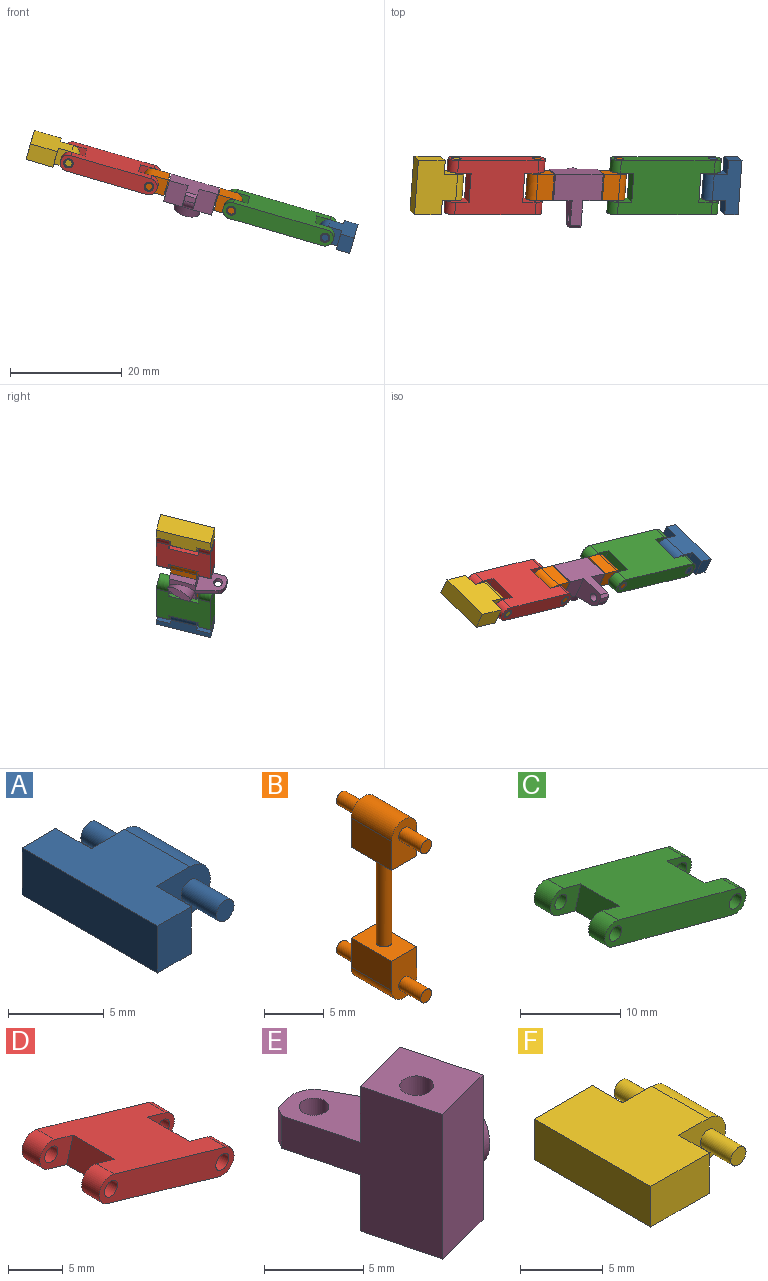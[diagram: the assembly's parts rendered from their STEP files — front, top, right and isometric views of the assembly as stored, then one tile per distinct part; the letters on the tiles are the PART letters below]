
ASSEMBLY  parts=6 mates=15
PART A: 14 faces, bbox 6.5x10x3 mm
  f0: plane 3x2.6mm, normal (1,0,0), area 7.8mm2, adj f2,f4,f6,f11
  f1: plane 3x2.6mm, normal (1,0,0), area 7.8mm2, adj f2,f4,f5,f10
  f2: plane 10x5mm, normal (0,0,1), area 37mm2, adj f0,f1,f3,f5,f6,f9,f10,f11
  f3: plane 10x3mm, normal (-1,0,0), area 30mm2, adj f2,f4,f5,f6
  f4: plane 10x5mm, normal (0,0,-1), area 37mm2, adj f0,f1,f3,f5,f6,f9,f10,f11
  f5: plane 3x2.5mm, normal (0,-1,0), area 7.5mm2, adj f1,f2,f3,f4
  f6: plane 3x2.5mm, normal (0,1,0), area 7.5mm2, adj f0,f2,f3,f4
  f7: cylinder r=0.65mm len=2.6mm, axis (0,1,0), area 10.6mm2, adj f8,f10
  f8: plane 1.3x1.3mm, normal (0,-1,0), area 1.3mm2, adj f7
  f9: cylinder r=1.5mm len=4.8mm, axis (0,1,0), area 22.6mm2, adj f2,f4,f10,f11
  f10: plane 4x3mm, normal (0,-1,0), area 9.7mm2, adj f1,f2,f4,f7,f9
  f11: plane 4x3mm, normal (0,1,0), area 9.7mm2, adj f0,f2,f4,f9,f13
  f12: plane 1.3x1.3mm, normal (0,1,0), area 1.3mm2, adj f13
  f13: cylinder r=0.65mm len=2.6mm, axis (0,1,0), area 10.6mm2, adj f11,f12
PART B: 21 faces, bbox 3x10x18.3 mm
  f0: cylinder r=0.65mm len=9.34mm, axis (0,0,-1), area 38.2mm2, adj f4,f14
  f1: plane 4.8x3mm, normal (1,0,0), area 14.4mm2, adj f2,f4,f5,f6
  f2: cylinder r=1.5mm len=4.8mm, axis (0,1,0), area 22.6mm2, adj f1,f3,f5,f6
  f3: plane 4.8x3mm, normal (-1,0,0), area 14.4mm2, adj f2,f4,f5,f6
  f4: plane 4.8x3mm, normal (0,0,-1), area 13.1mm2, adj f0,f1,f3,f5,f6
  f5: plane 4.5x3mm, normal (0,-1,0), area 11.2mm2, adj f1,f2,f3,f4,f10
  f6: plane 4.5x3mm, normal (0,1,0), area 11.2mm2, adj f1,f2,f3,f4,f8
  f7: plane 1.3x1.3mm, normal (0,1,0), area 1.3mm2, adj f8
  f8: cylinder r=0.65mm len=2.6mm, axis (0,1,0), area 10.6mm2, adj f6,f7
  f9: plane 1.3x1.3mm, normal (0,-1,0), area 1.3mm2, adj f10
  f10: cylinder r=0.65mm len=2.6mm, axis (0,1,0), area 10.6mm2, adj f5,f9
  f11: plane 4.8x3mm, normal (-1,0,0), area 14.4mm2, adj f12,f14,f15,f16
  f12: cylinder r=1.5mm len=4.8mm, axis (0,1,0), area 22.6mm2, adj f11,f13,f15,f16
  f13: plane 4.8x3mm, normal (1,0,0), area 14.4mm2, adj f12,f14,f15,f16
  f14: plane 4.8x3mm, normal (0,0,1), area 13.1mm2, adj f0,f11,f13,f15,f16
  f15: plane 4.5x3mm, normal (0,-1,0), area 11.2mm2, adj f11,f12,f13,f14,f20
  f16: plane 4.5x3mm, normal (0,1,0), area 11.2mm2, adj f11,f12,f13,f14,f18
  f17: plane 1.3x1.3mm, normal (0,1,0), area 1.3mm2, adj f18
  f18: cylinder r=0.65mm len=2.6mm, axis (0,1,0), area 10.6mm2, adj f16,f17
  f19: plane 1.3x1.3mm, normal (0,-1,0), area 1.3mm2, adj f20
  f20: cylinder r=0.65mm len=2.6mm, axis (0,1,0), area 10.6mm2, adj f15,f19
PART C: 18 faces, bbox 19.9x10x7.5 mm
  f0: plane 5.4x2.9mm, normal (-0.97,0,0.26), area 16.2mm2, adj f2,f3,f11,f17
  f1: plane 5.4x2.9mm, normal (0.97,0,-0.26), area 16.2mm2, adj f2,f3,f8,f14
  f2: plane 16.9x10mm, normal (0.26,0,0.97), area 148mm2, adj f0,f1,f4,f5,f6,f8,f9,f11
  f3: plane 16.9x10mm, normal (-0.26,0,-0.97), area 148mm2, adj f0,f1,f4,f5,f6,f8,f9,f11
  f4: plane 19.9x7.53mm, normal (0,-1,0), area 55mm2, adj f2,f3,f6,f7,f9,f10
  f5: plane 19.9x7.53mm, normal (0,1,0), area 55mm2, adj f2,f3,f12,f13,f15,f16
  f6: cylinder r=1.5mm len=2.95mm, axis (0,-1,0), area 10.8mm2, adj f2,f3,f4,f8
  f7: cylinder r=0.85mm len=2.3mm, axis (0,-1,0), area 12.3mm2, adj f4,f8
  f8: plane 4.3x3.6mm, normal (0,1,0), area 8.8mm2, adj f1,f2,f3,f6,f7
  f9: cylinder r=1.5mm len=2.95mm, axis (0,-1,0), area 10.8mm2, adj f2,f3,f4,f11
  f10: cylinder r=0.85mm len=2.3mm, axis (0,-1,0), area 12.3mm2, adj f4,f11
  f11: plane 4.3x3.6mm, normal (0,1,0), area 8.8mm2, adj f0,f2,f3,f9,f10
  f12: cylinder r=1.5mm len=2.95mm, axis (0,1,0), area 10.8mm2, adj f2,f3,f5,f14
  f13: cylinder r=0.85mm len=2.3mm, axis (0,1,0), area 12.3mm2, adj f5,f14
  f14: plane 4.3x3.6mm, normal (0,-1,0), area 8.8mm2, adj f1,f2,f3,f12,f13
  f15: cylinder r=1.5mm len=2.95mm, axis (0,1,0), area 10.8mm2, adj f2,f3,f5,f17
  f16: cylinder r=0.85mm len=2.3mm, axis (0,1,0), area 12.3mm2, adj f5,f17
  f17: plane 4.3x3.6mm, normal (0,-1,0), area 8.8mm2, adj f0,f2,f3,f15,f16
PART D: 18 faces, bbox 17.4x10x7.2 mm
  f0: plane 5.4x2.88mm, normal (-0.96,0,0.28), area 16.2mm2, adj f2,f3,f8,f14
  f1: plane 5.4x2.88mm, normal (0.96,0,-0.28), area 16.2mm2, adj f2,f3,f11,f17
  f2: plane 14.4x10mm, normal (0.28,0,0.96), area 123mm2, adj f0,f1,f4,f5,f6,f8,f9,f11
  f3: plane 14.4x10mm, normal (-0.28,0,-0.96), area 123mm2, adj f0,f1,f4,f5,f6,f8,f9,f11
  f4: plane 17.4x7.19mm, normal (0,-1,0), area 47.5mm2, adj f2,f3,f6,f7,f9,f10
  f5: plane 17.4x7.19mm, normal (0,1,0), area 47.5mm2, adj f2,f3,f12,f13,f15,f16
  f6: cylinder r=1.5mm len=2.94mm, axis (0,-1,0), area 10.8mm2, adj f2,f3,f4,f8
  f7: cylinder r=0.85mm len=2.3mm, axis (0,-1,0), area 12.3mm2, adj f4,f8
  f8: plane 4.32x3.64mm, normal (0,1,0), area 8.8mm2, adj f0,f2,f3,f6,f7
  f9: cylinder r=1.5mm len=2.94mm, axis (0,-1,0), area 10.8mm2, adj f2,f3,f4,f11
  f10: cylinder r=0.85mm len=2.3mm, axis (0,-1,0), area 12.3mm2, adj f4,f11
  f11: plane 4.32x3.64mm, normal (0,1,0), area 8.8mm2, adj f1,f2,f3,f9,f10
  f12: cylinder r=1.5mm len=2.94mm, axis (0,1,0), area 10.8mm2, adj f2,f3,f5,f14
  f13: cylinder r=0.85mm len=2.3mm, axis (0,1,0), area 12.3mm2, adj f5,f14
  f14: plane 4.32x3.64mm, normal (0,-1,0), area 8.8mm2, adj f0,f2,f3,f12,f13
  f15: cylinder r=1.5mm len=2.94mm, axis (0,1,0), area 10.8mm2, adj f2,f3,f5,f17
  f16: cylinder r=0.85mm len=2.3mm, axis (0,1,0), area 12.3mm2, adj f5,f17
  f17: plane 4.32x3.64mm, normal (0,-1,0), area 8.8mm2, adj f1,f2,f3,f15,f16
PART E: 18 faces, bbox 6.7x10x8.9 mm
  f0: plane 4.65x4.45mm, normal (0.97,0.25,0), area 12.6mm2, adj f2,f4,f7,f9,f15
  f1: plane 3.87x3.45mm, normal (-0.25,0.97,0), area 13.8mm2, adj f3,f6,f8,f13
  f2: plane 3.87x3.45mm, normal (-0.25,0.97,0), area 13.8mm2, adj f0,f3,f7,f14
  f3: plane 9.1x8.9mm, normal (-0.97,-0.25,0), area 51.9mm2, adj f1,f2,f4,f6,f7,f13,f14,f17
  f4: plane 8.9x3.87mm, normal (0.25,-0.97,0), area 35.6mm2, adj f0,f3,f6,f7,f8
  f5: cylinder r=0.85mm len=8.9mm, axis (0,0,-1), area 47.5mm2, adj f6,f7
  f6: plane 5.64x5.07mm, normal (0,0,1), area 16.9mm2, adj f1,f3,f4,f5,f8
  f7: plane 5.64x5.07mm, normal (0,0,-1), area 16.9mm2, adj f0,f2,f3,f4,f5
  f8: plane 4.65x4.45mm, normal (0.97,0.25,0), area 12.6mm2, adj f1,f4,f6,f9,f15
  f9: plane 3.6x2.01mm, normal (0.87,0.49,0), area 8.2mm2, adj f0,f8,f10,f13,f14
  f10: cylinder r=1.5mm len=2mm, axis (0,0,-1), area 3.9mm2, adj f9,f12,f13,f14
  f11: cylinder r=0.75mm len=2mm, axis (0,0,-1), area 9.4mm2, adj f13,f14
  f12: plane 2x0.97mm, normal (-0.25,0.97,0), area 2mm2, adj f10,f13,f14,f17
  f13: plane 5.36x5.02mm, normal (0,0,1), area 14.8mm2, adj f1,f3,f9,f10,f11,f12,f17
  f14: plane 5.36x5.02mm, normal (0,0,-1), area 14.8mm2, adj f2,f3,f9,f10,f11,f12,f17
  f15: cylinder r=2.32mm len=4.65mm, axis (-1,0,0), area 15.8mm2, adj f0,f8,f16
  f16: plane 4.65x4.65mm, normal (1,0,0), area 17mm2, adj f15
  f17: plane 2x0.61mm, normal (-0.86,0.51,0), area 1.4mm2, adj f3,f12,f13,f14
PART F: 14 faces, bbox 9x10x3 mm
  f0: plane 3x2.6mm, normal (1,0,0), area 7.8mm2, adj f2,f4,f6,f10
  f1: plane 3x2.6mm, normal (1,0,0), area 7.8mm2, adj f2,f4,f5,f11
  f2: plane 10x7.5mm, normal (0,0,1), area 62mm2, adj f0,f1,f3,f5,f6,f9,f10,f11
  f3: plane 10x3mm, normal (-1,0,0), area 30mm2, adj f2,f4,f5,f6
  f4: plane 10x7.5mm, normal (0,0,-1), area 62mm2, adj f0,f1,f3,f5,f6,f9,f10,f11
  f5: plane 5x3mm, normal (0,-1,0), area 15mm2, adj f1,f2,f3,f4
  f6: plane 5x3mm, normal (0,1,0), area 15mm2, adj f0,f2,f3,f4
  f7: cylinder r=0.65mm len=2.6mm, axis (0,1,0), area 10.6mm2, adj f8,f10
  f8: plane 1.3x1.3mm, normal (0,1,0), area 1.3mm2, adj f7
  f9: cylinder r=1.5mm len=4.8mm, axis (0,-1,0), area 22.6mm2, adj f2,f4,f10,f11
  f10: plane 4x3mm, normal (0,1,0), area 9.7mm2, adj f0,f2,f4,f7,f9
  f11: plane 4x3mm, normal (0,-1,0), area 9.7mm2, adj f1,f2,f4,f9,f13
  f12: plane 1.3x1.3mm, normal (0,-1,0), area 1.3mm2, adj f13
  f13: cylinder r=0.65mm len=2.6mm, axis (0,1,0), area 10.6mm2, adj f11,f12
PLACE A rot(axis=(-0.02,-0.99,-0.13),163.9deg) t=(6.64,33.66,-28.3)mm
PLACE B rot(axis=(-0.6,-0.08,0.8),168.5deg) t=(-25.46,23.86,20.77)mm
PLACE C rot(axis=(-0.03,-0.99,-0.12),178.8deg) t=(10.79,33.05,-27.04)mm
PLACE D rot(axis=(-0.96,0,0.28),165.6deg) t=(-50.91,29.23,6.37)mm
PLACE E rot(axis=(-0.59,-0.15,0.79),157deg) t=(-26.09,18.17,18.61)mm
PLACE F rot(axis=(-0.99,0.02,0.14),165.7deg) t=(-52.05,29.93,3.89)mm
MATE cylindrical F.f7 <-> D.f7  axis (0.07,0.97,0.24) through (-42.1,34.77,2.29)mm
MATE cylindrical C.f6 <-> B.f12  axis (-0.07,-0.97,-0.24) through (-13.12,32.54,-6.73)mm
MATE planar C.f3 <-> D.f3  axis (0.27,-0.25,0.93) through (-4.5,29.55,-8.42)mm
MATE planar B.f3 <-> D.f3  axis (0.27,-0.25,0.93) through (-26.19,29.55,-2.12)mm
MATE planar A.f2 <-> C.f2  axis (-0.27,0.25,-0.93) through (5.91,30.3,-14.47)mm
MATE parallel A.f3 <-> E.f5  axis (0.96,0,-0.28) through (7.89,30.3,-15.05)mm
MATE planar D.f3 <-> F.f4  axis (0.27,-0.25,0.93) through (-34.84,29.55,0.4)mm
MATE planar A.f5 <-> C.f4  axis (-0.07,-0.97,-0.24) through (6.75,25.08,-14.5)mm
MATE cylindrical A.f7 <-> C.f9  axis (-0.07,-0.97,-0.24) through (3.33,27.6,-12.83)mm
MATE cylindrical D.f9 <-> B.f2  axis (0.07,0.97,0.24) through (-27.69,34.77,-1.9)mm
MATE planar C.f5 <-> B.f12  axis (0.07,0.97,0.24) through (-4.56,34.77,-8.62)mm
MATE planar F.f7 <-> D.f4  axis (0.07,0.97,0.24) through (-42.1,34.77,2.29)mm
MATE cylindrical E.f5 <-> B.f0  axis (0.96,0,-0.28) through (-24.93,29.93,-4)mm
MATE planar E.f3 <-> D.f3  axis (0.27,-0.25,0.93) through (-20.3,28.75,-4.04)mm
MATE planar B.f2 <-> D.f4  axis (0.07,0.97,0.24) through (-27.69,34.77,-1.9)mm
